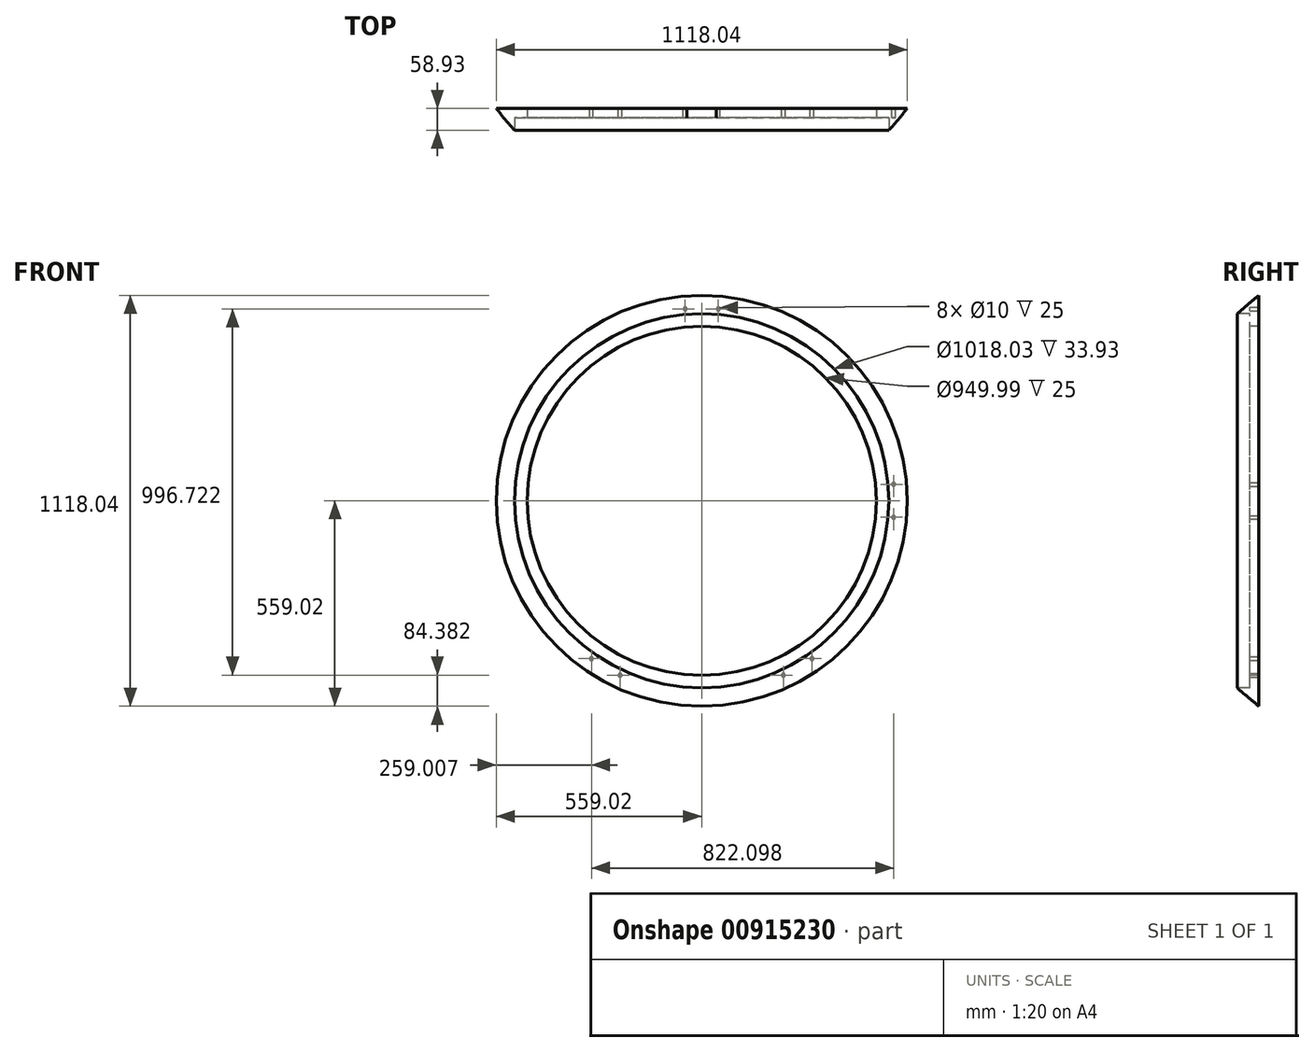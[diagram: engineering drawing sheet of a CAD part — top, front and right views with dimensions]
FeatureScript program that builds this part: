
annotation { "Feature Type Name" : "Feature", "Feature Type Description" : "" }
export const myFeature = defineFeature(function(context is Context, id is Id, definition is map)
    precondition{}
    {
        {
            var Q0;
            Q0=qCreatedBy(makeId("Front.planeOp"),FACE);
            var sketch = newSketch(context, id + "F0", { "sketchPlane" : qUnion([Q0])});
            skLineSegment(sketch, "E0", {"start": v(0, 559.01) * mm, "end": v(0, -559.01) * mm, "construction": true});
            skLineSegment(sketch, "E1", {"start": v(-559.01, 0) * mm, "end": v(559.01, 0) * mm, "construction": true});
            skCircle(sketch, "E2", {"center": v(0, 0) * mm, "radius": 559.01 * mm, "construction": true});
            skSolve(sketch);
        }
        {
            var Q0;
            Q0=qCreatedBy(makeId("Top.planeOp"),FACE);
            var sketch = newSketch(context, id + "F1", { "sketchPlane" : qUnion([Q0])});
            skLineSegment(sketch, "E3", {"start": v(0, -37.08) * mm, "end": v(0, 39.58) * mm, "construction": true});
            skLineSegment(sketch, "E4", {"start": v(-475, 0) * mm, "end": v(-559.01, 0) * mm});
            skLineSegment(sketch, "E5", {"start": v(-475, 0) * mm, "end": v(-475, -25) * mm, "construction": true});
            skLineSegment(sketch, "E6", {"start": v(-475, -25) * mm, "end": v(-509.02, -25) * mm, "construction": true});
            skLineSegment(sketch, "E7", {"start": v(-509.02, -25) * mm, "end": v(-509.02, -58.93) * mm, "construction": true});
            skLineSegment(sketch, "E8", {"start": v(-475, 0) * mm, "end": v(-475, -25) * mm});
            skLineSegment(sketch, "E9", {"start": v(-475, -25) * mm, "end": v(-509.02, -25) * mm});
            skLineSegment(sketch, "E10", {"start": v(-509.02, -25) * mm, "end": v(-509.02, -58.93) * mm});
            skFitSpline(sketch, "E11", {"points": [v(-559.01, 0) * mm, v(-528.05, -37.81) * mm, v(-488.46, -80.8) * mm], "startDerivative": vector(62.22, -78.4) * mm, "endDerivative": vector(78.65, -83.14) * mm});
            skSolve(sketch);
        }
        {
            var Q0;
            Q0=makeQuery(id+"F1.imprint","IMPRINT",FACE,{"disambiguationData":[TD([[makeQuery(id+"F1.imprint","IMPRINT",EDGE,{"derivedFrom":sQuery(id+"F1.wireOp",EDGE,"E4")}),1.0]])]});
            var Q1;
            Q1=sQuery(id+"F1.wireOp",EDGE,"E3");
            revolve(context, id + "F2", {"surfaceOperationType" : NewSurfaceOperationType.NEW, "entities" : qUnion([Q0]), "axis" : qUnion([Q1]), "revolveType" : RevolveType.FULL});
        }
        {
            var Q0;
            Q0=qCreatedBy(makeId("Front.planeOp"),FACE);
            var sketch = newSketch(context, id + "F3", { "sketchPlane" : qUnion([Q0])});
            skLineSegment(sketch, "E12", {"start": v(0, 0) * mm, "end": v(0, 524.02) * mm, "construction": true});
            skCircle(sketch, "E13", {"center": v(0, 0) * mm, "radius": 524.02 * mm, "construction": true});
            skLineSegment(sketch, "E14", {"start": v(0, 429.05) * mm, "end": v(-45, 429.05) * mm, "construction": true});
            skLineSegment(sketch, "E15", {"start": v(-45, 429.05) * mm, "end": v(-45, 522.08) * mm, "construction": true});
            skCircle(sketch, "E16", {"center": v(-45, 522.08) * mm, "radius": 5 * mm});
            skLineSegment(sketch, "E17", {"start": v(0, 429.05) * mm, "end": v(45, 429.05) * mm, "construction": true});
            skLineSegment(sketch, "E18", {"start": v(45, 429.05) * mm, "end": v(45, 522.08) * mm, "construction": true});
            skCircle(sketch, "E19", {"center": v(45, 522.08) * mm, "radius": 5 * mm});
            skLineSegment(sketch, "E20", {"start": v(428.6, 0) * mm, "end": v(428.6, 45) * mm, "construction": true});
            skLineSegment(sketch, "E21", {"start": v(428.6, 0) * mm, "end": v(428.6, -45) * mm, "construction": true});
            skLineSegment(sketch, "E22", {"start": v(428.6, 45) * mm, "end": v(522.08, 45) * mm, "construction": true});
            skLineSegment(sketch, "E23", {"start": v(428.6, -45) * mm, "end": v(522.08, -45) * mm, "construction": true});
            skCircle(sketch, "E24", {"center": v(522.08, 45) * mm, "radius": 5 * mm});
            skCircle(sketch, "E25", {"center": v(522.08, -45) * mm, "radius": 5 * mm});
            skLineSegment(sketch, "E26", {"start": v(0, 0) * mm, "end": v(262, -453.81) * mm, "construction": true});
            skLineSegment(sketch, "E27", {"start": v(209.29, -362.5) * mm, "end": v(248.26, -340) * mm, "construction": true});
            skLineSegment(sketch, "E28", {"start": v(209.29, -362.5) * mm, "end": v(170.32, -385) * mm, "construction": true});
            skLineSegment(sketch, "E29", {"start": v(248.26, -340) * mm, "end": v(300.01, -429.64) * mm, "construction": true});
            skLineSegment(sketch, "E30", {"start": v(170.32, -385) * mm, "end": v(222.07, -474.64) * mm, "construction": true});
            skCircle(sketch, "E31", {"center": v(300.01, -429.64) * mm, "radius": 5 * mm});
            skCircle(sketch, "E32", {"center": v(222.07, -474.64) * mm, "radius": 5 * mm});
            skLineSegment(sketch, "E33", {"start": v(0, 0) * mm, "end": v(-262.01, -453.81) * mm, "construction": true});
            skLineSegment(sketch, "E34", {"start": v(-197.77, -342.54) * mm, "end": v(-158.8, -365.04) * mm, "construction": true});
            skLineSegment(sketch, "E35", {"start": v(-197.77, -342.54) * mm, "end": v(-236.74, -320.04) * mm, "construction": true});
            skLineSegment(sketch, "E36", {"start": v(-158.8, -365.04) * mm, "end": v(-222.07, -474.64) * mm, "construction": true});
            skLineSegment(sketch, "E37", {"start": v(-236.74, -320.04) * mm, "end": v(-300.01, -429.64) * mm, "construction": true});
            skCircle(sketch, "E38", {"center": v(-222.07, -474.64) * mm, "radius": 5 * mm});
            skCircle(sketch, "E39", {"center": v(-300.01, -429.64) * mm, "radius": 5 * mm});
            skSolve(sketch);
        }
        {
            var Q0;
            Q0=makeQuery(id+"F3.imprint","IMPRINT",FACE,{"disambiguationData":[TD([[makeQuery(id+"F3.imprint","IMPRINT",EDGE,{"derivedFrom":sQuery(id+"F3.wireOp",EDGE,"E39")}),1.0]])]});
            var Q1;
            Q1=makeQuery(id+"F3.imprint","IMPRINT",FACE,{"disambiguationData":[TD([[makeQuery(id+"F3.imprint","IMPRINT",EDGE,{"derivedFrom":sQuery(id+"F3.wireOp",EDGE,"E38")}),1.0]])]});
            var Q2;
            Q2=makeQuery(id+"F3.imprint","IMPRINT",FACE,{"disambiguationData":[TD([[makeQuery(id+"F3.imprint","IMPRINT",EDGE,{"derivedFrom":sQuery(id+"F3.wireOp",EDGE,"E32")}),1.0]])]});
            var Q3;
            Q3=makeQuery(id+"F3.imprint","IMPRINT",FACE,{"disambiguationData":[TD([[makeQuery(id+"F3.imprint","IMPRINT",EDGE,{"derivedFrom":sQuery(id+"F3.wireOp",EDGE,"E31")}),1.0]])]});
            var Q4;
            Q4=makeQuery(id+"F3.imprint","IMPRINT",FACE,{"disambiguationData":[TD([[makeQuery(id+"F3.imprint","IMPRINT",EDGE,{"derivedFrom":sQuery(id+"F3.wireOp",EDGE,"E24")}),1.0]])]});
            var Q5;
            Q5=makeQuery(id+"F3.imprint","IMPRINT",FACE,{"disambiguationData":[TD([[makeQuery(id+"F3.imprint","IMPRINT",EDGE,{"derivedFrom":sQuery(id+"F3.wireOp",EDGE,"E25")}),1.0]])]});
            var Q6;
            Q6=makeQuery(id+"F3.imprint","IMPRINT",FACE,{"disambiguationData":[TD([[makeQuery(id+"F3.imprint","IMPRINT",EDGE,{"derivedFrom":sQuery(id+"F3.wireOp",EDGE,"E19")}),1.0]])]});
            var Q7;
            Q7=makeQuery(id+"F3.imprint","IMPRINT",FACE,{"disambiguationData":[TD([[makeQuery(id+"F3.imprint","IMPRINT",EDGE,{"derivedFrom":sQuery(id+"F3.wireOp",EDGE,"E16")}),1.0]])]});
            extrude(context, id + "F4", {"entities" : qUnion([Q0, Q1, Q2, Q3, Q4, Q5, Q6, Q7]), "operationType" : NewBodyOperationType.REMOVE, "depth" : 25 * mm, "offsetDistance" : 25 * mm});
        }
    });
